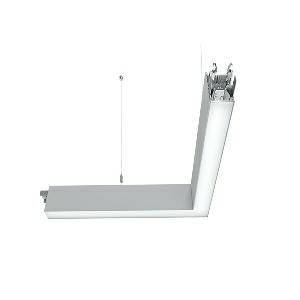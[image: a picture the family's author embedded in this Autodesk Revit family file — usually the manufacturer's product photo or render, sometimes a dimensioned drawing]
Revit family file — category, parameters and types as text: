
# Revit family: dotoo_line_-_dlp_1500_830_d_ll_mid_00807698_4a40
name_source: partatom
category: Lighting Fixtures
units: mm (PartAtom-declared; Revit-internal decimal feet)

## family parameters
Cut with Voids When Loaded = No
Host = Face
Light Source = No
Part Type = Normal
Room Calculation Point = No
Round Connector Dimension = Use Diameter
Shared = No

## types (1)
- DOTOO.line - DLP 1500/830/D/LL MID (1 x LED, 1300 lm, 3000K)
    Apparent Load = 13 VA
    Approval mark = CE
    CIE Flux Codes = 67 91 98 100 100
    Color Rendering = 80-89
    Color Temperature = 3000K
    Control Gear = Electronic ballast
    Default Elevation = 1800 mm
    Description = DLP 1500/830/D|Suspended luminaire|light source: LED|connected load: 220-240V, 50/60Hz|Power consumption: approx. 13 W|standby: approx. 0,20|luminous flux: 1300 lm|luminous efficacy: 100 lm/W|light distribution: Direct|direct ratio: approx. 100 %|colour temperature: Warm white, ca. 3000 K|color rendering index (CRI): >= 80|chromaticity tolerance:  3 SDCM|System of protection: IP 40|technology: Continuously dimmable|luminaire body|material: Sectional aluminium|colour: Silver|lamp cover: Acrylic (PMMA), Clear|Fastening: Steel cable 0.3 - 0.7 m|glare control: Prism aperture|luminance(L65): <= 3000 cd/m|unified glare rating(4H 8H): <=  19|special features: DALI Load 1x, TouchDIM - dimming via standard switch, Through-wired, up to 18 m on one mains connection, Flicker-free, Continous light without dark z, 90░ rerouting on the left side, Suitable as emergency lighting, Mechanical and electrical connection of the individual modules without tools|
    Frequency = 50 Hz
    Height = 110 mm
    Lamp = 1 x LED
    Lamp Light Flux = 1300 lm
    Lamp count = 1
    Length = 600 mm
    Luminous efficacy = 100 lm/W
    Manufacturer = Waldmann
    ModVariant = No
    Model = 00807698
    Mounting Place = Ceiling
    Mounting Type = Pendant
    Number of Poles = 1
    OnlyDefault = Yes
    Power Factor = 1
    Product Name = DOTOO.line - DLP 1500/830/D/LL MID
    Product group = Suspended luminaire
    ProductGroupID = 9
    Protection Class = Protection class I
    Protection Degree = IP 40
    RLX_Detail_Level = 1
    RLX_Emergency_Light_Flux = 0 lm
    RLX_Emergency_Type = 0
    RLX_Emergency_Type_DB = No
    RlxData = <blob elided: 21889 chars, md5=18dade65>
    Socket = socket
    Standby Power = 0 W
    System Light Flux = 1300 lm
    System Power = 13 W
    Type Comments = Product without accessories
    Type Image = ilp_dlp_ll_si.jpg
    URL = http://relux.com
    VarID = ---
    Voltage = 230 V
    Voltage Range = 220-240 V
    Weight = 0.00 kg
    Width = 600 mm

## geometry (parser evidence)
native form markers: Blend x4, Sweep x11
no freeform markers — native parametric forms only
